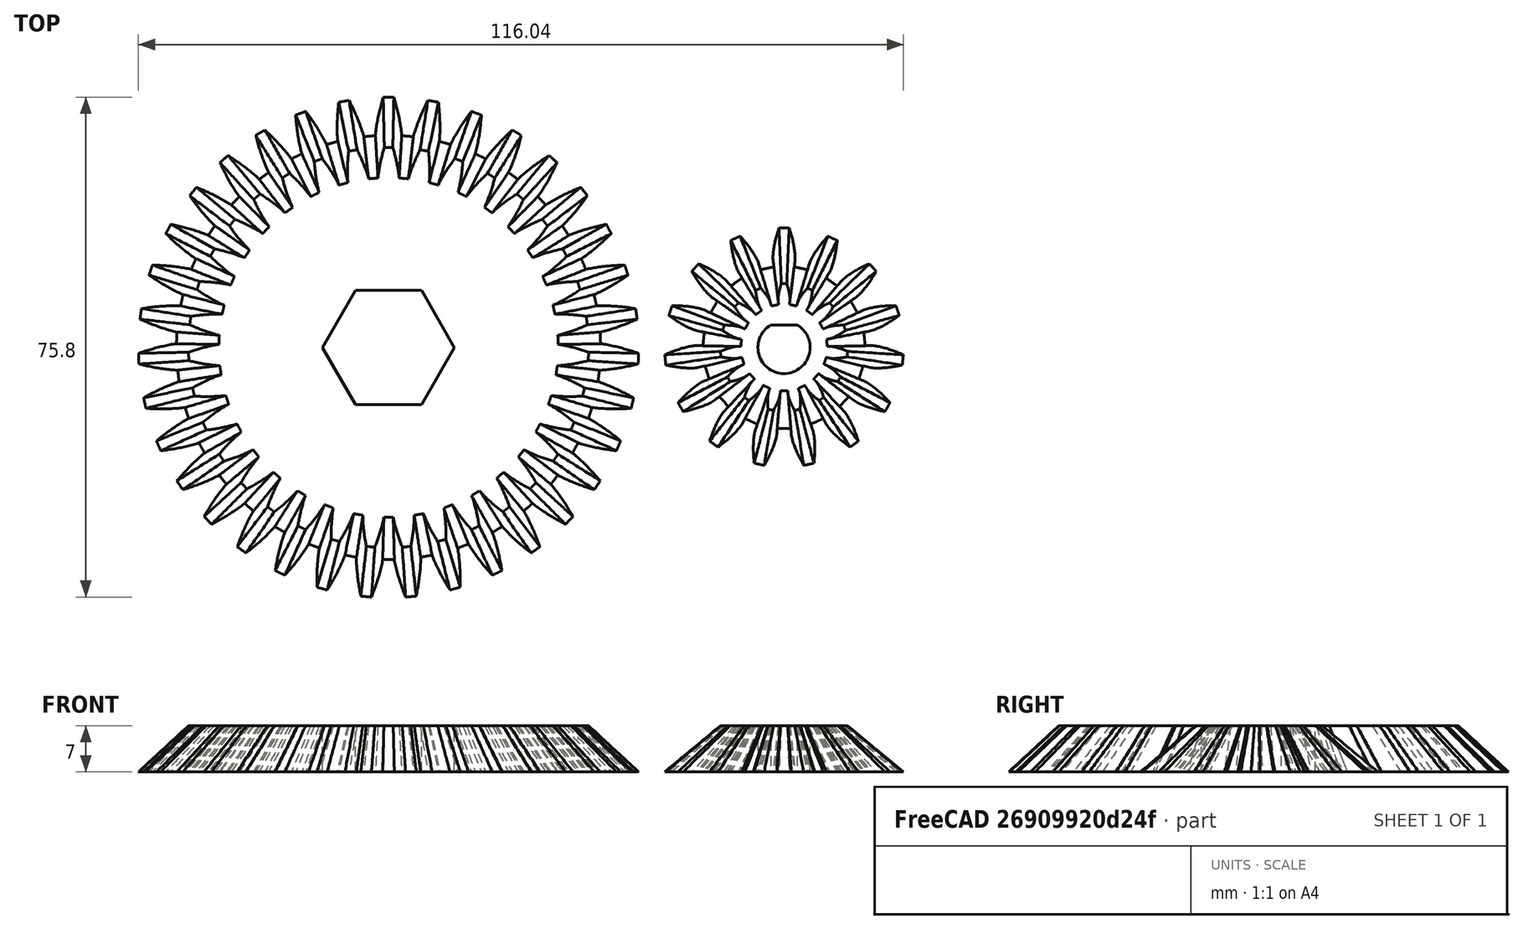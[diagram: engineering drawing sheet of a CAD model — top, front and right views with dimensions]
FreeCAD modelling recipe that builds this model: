
FCSTD DOCUMENT  (FreeCAD 0.20R29603 (Git))
Label: getriebe
License: All rights reserved
LicenseURL: http://en.wikipedia.org/wiki/All_rights_reserved
objects: TechDraw::DrawViewDimension×3, PartDesign::FeaturePython×2, PartDesign::Body×2, TechDraw::DrawViewPart×2, TechDraw::DrawViewAnnotation×2, PartDesign::SubtractivePrism×1, PartDesign::SubtractiveCylinder×1, PartDesign::AdditiveBox×1, TechDraw::DrawSVGTemplate×1, TechDraw::DrawViewDetail×1, TechDraw::DrawPage×1
note: 10 computed .brp shape members not serialized (recipe doc carries the construction recipe); baked Part::Feature solids carry a one-line shape summary decoded from their .brp

FEATURE [PartDesign::FeaturePython] BevelGear  # WARN: FeaturePython — macro-defined, semantics opaque (R4)
  AttacherType = Attacher::AttachEngine3D
  angular_backlash = 0
  backlash = 0
  beta = 0
  clearance = 0.1
  dw = 70
  height = 7
  module = 2
  numpoints = 6
  pitch_angle = 45
  pressure_angle = 20
  reset_origin = true
  teeth = 35
  version = 0.0.4
  expr: angular_backlash = backlash / dw * 360 ° / pi
  expr: dw = teeth * module
FEATURE [PartDesign::SubtractivePrism] Prism
  AttacherType = Attacher::AttachEngine3D
  BaseFeature = -> BevelGear
  Circumradius = 10
  FirstAngle = 0
  Height = 7
  MapMode = 45
  Placement = pos=(2.5e-15,-6.4e-15,0) rot=(0,0,1;0rad)
  Polygon = 6
  SecondAngle = 0
  Support = -> [BevelGear]
FEATURE [PartDesign::Body] Body  label="Zahnrad Eisdosierer"
  Group = -> [BevelGear,Prism]
  Origin = -> Origin
  Tip = -> Prism
FEATURE [PartDesign::FeaturePython] BevelGear001  # WARN: FeaturePython — macro-defined, semantics opaque (R4)
  AttacherType = Attacher::AttachEngine3D
  angular_backlash = 0
  backlash = 0
  beta = 0
  clearance = 0.1
  dw = 30
  height = 7
  module = 2
  numpoints = 6
  pitch_angle = 45
  pressure_angle = 20
  reset_origin = true
  teeth = 15
  version = 0.0.4
  expr: angular_backlash = backlash / dw * 360 ° / pi
  expr: dw = teeth * module
FEATURE [PartDesign::SubtractiveCylinder] Cylinder
  Angle = 360
  AttacherType = Attacher::AttachEngine3D
  BaseFeature = -> BevelGear001
  FirstAngle = 0
  Height = 7
  MapMode = 45
  Placement = pos=(5e-15,-4.3e-15,0) rot=(0,0,1;0rad)
  Radius = 3.96
  SecondAngle = 0
  Support = -> [BevelGear001]
FEATURE [PartDesign::AdditiveBox] Box
  AttacherType = Attacher::AttachEngine3D
  AttachmentOffset = pos=(3.42,-3.5,-7) rot=(0,0,1;0rad)
  BaseFeature = -> Cylinder
  Height = 7
  Length = 0.54
  MapMode = 11
  Placement = pos=(3.5,3.42,0) rot=(0,0,1;1.5708rad)
  Support = -> [Cylinder]
  Width = 7
FEATURE [PartDesign::Body] Body001  label="zahnrad motor"
  Group = -> [BevelGear001,Cylinder,Box]
  Origin = -> Origin001
  Placement = pos=(60,0,0) rot=(0,0,1;0rad)
  Tip = -> Box
FEATURE [TechDraw::DrawSVGTemplate] Template
  EditableTexts = Designed_by_Name=B. Schulze; Drawing_number=1; FC-Date=03.08.2023; FC-SC=1:1; FC-SH=5; FC-Title=Eisdosierer; Subtitle=Getriebe; Weight=0
  Height = 210
  Orientation = 1
  Width = 297
FEATURE [TechDraw::DrawViewPart] View  label="Groß"
  Caption = Großes Kegelrad
  CoarseView = false
  Direction = (0,0.001,1)
  Focus = 100
  HardHidden = false
  IsoCount = 0
  IsoHidden = false
  IsoVisible = false
  LockPosition = false
  Perspective = false
  Rotation = 0
  ScaleType = 0
  SeamHidden = false
  SeamVisible = true
  SmoothHidden = false
  SmoothVisible = true
  Source = -> [Body]
  X = 55.9286
  XDirection = (1,0,0)
  Y = 133.249
FEATURE [TechDraw::DrawViewDimension] Dimension
  AngleOverride = false
  Arbitrary = false
  ArbitraryTolerances = false
  EqualTolerance = true
  ExtensionAngle = 0
  FormatSpec = %.2w
  FormatSpecOverTolerance = %+.2w
  FormatSpecUnderTolerance = %+.2w
  Inverted = false
  LineAngle = 0
  LockPosition = false
  MeasureType = 1
  OverTolerance = 0
  References2D = -> [View]
  Rotation = 0
  ScaleType = 0
  TheoreticalExact = false
  Type = 1
  UnderTolerance = 0
  X = 0.611389
  Y = 20.8292
FEATURE [TechDraw::DrawViewAnnotation] Annotation
  Font = osifont
  LineSpace = 80
  LockPosition = false
  MaxWidth = -1
  Rotation = 0
  ScaleType = 0
  Text = Großes Kegelrad | - Höhe: 7 mm | - Module: 2 mm | - Zähne: 35
  TextSize = 5
  TextStyle = 0
  X = 121.671
  Y = 131.49
FEATURE [TechDraw::DrawViewPart] View001  label="Klein"
  Caption = Kleines Kegelrad
  CoarseView = false
  Direction = (0,0.001,1)
  Focus = 100
  HardHidden = false
  IsoCount = 0
  IsoHidden = false
  IsoVisible = false
  LockPosition = false
  Perspective = false
  Rotation = 0
  ScaleType = 0
  SeamHidden = false
  SeamVisible = true
  SmoothHidden = false
  SmoothVisible = true
  Source = -> [Body001]
  X = 173.631
  XDirection = (1,0,0)
  Y = 130.878
FEATURE [TechDraw::DrawViewDetail] Detail
  AnchorPoint = (0,0,0)
  BaseView = -> View001
  CoarseView = false
  Direction = (0,0.001,1)
  Focus = 100
  HardHidden = false
  IsoCount = 0
  IsoHidden = false
  IsoVisible = false
  LockPosition = false
  Perspective = false
  Radius = 6
  Reference = 1
  Rotation = 0
  Scale = 2
  ScaleType = 2
  SeamHidden = false
  SeamVisible = true
  SmoothHidden = false
  SmoothVisible = true
  Source = -> [Body001]
  X = 214.113
  XDirection = (1,0,0)
  Y = 130.403
FEATURE [TechDraw::DrawViewAnnotation] Annotation001
  Font = osifont
  LineSpace = 80
  LockPosition = false
  MaxWidth = -1
  Rotation = 0
  ScaleType = 0
  Text = Kleines Kegelrad | - Höhe: 7 mm | - Module: 2 mm | - Zähne: 15
  TextSize = 5
  TextStyle = 0
  X = 257.718
  Y = 134.75
FEATURE [TechDraw::DrawViewDimension] Dimension001
  AngleOverride = false
  Arbitrary = false
  ArbitraryTolerances = false
  EqualTolerance = true
  ExtensionAngle = 0
  FormatSpec = %.2w
  FormatSpecOverTolerance = %+.2w
  FormatSpecUnderTolerance = %+.2w
  Inverted = false
  LineAngle = 0
  LockPosition = false
  MeasureType = 1
  OverTolerance = 0
  References2D = -> [Detail]
  Rotation = 0
  ScaleType = 0
  TheoreticalExact = false
  Type = 1
  UnderTolerance = 0
  X = 0.189558
  Y = 23.025
FEATURE [TechDraw::DrawViewDimension] Dimension002
  AngleOverride = false
  Arbitrary = false
  ArbitraryTolerances = false
  EqualTolerance = true
  ExtensionAngle = 0
  FormatSpec = %.2w
  FormatSpecOverTolerance = %+.2w
  FormatSpecUnderTolerance = %+.2w
  Inverted = false
  LineAngle = 0
  LockPosition = false
  MeasureType = 1
  OverTolerance = 0
  References2D = -> [Detail]
  Rotation = 0
  ScaleType = 0
  TheoreticalExact = false
  Type = 1
  UnderTolerance = 0
  X = -0.423606
  Y = -10.947
FEATURE [TechDraw::DrawPage] Page
  KeepUpdated = true
  NextBalloonIndex = 2
  ProjectionType = 0
  Template = -> Template
  Views = -> [View,Dimension,Annotation,View001,Detail,Annotation001,Dimension001,Dimension002]
